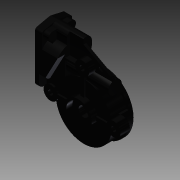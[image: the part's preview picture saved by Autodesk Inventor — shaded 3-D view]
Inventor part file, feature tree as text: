
AUTODESK INVENTOR PART (.ipt)
format: ipt  version: 2015 SP1 (Build 190203100, 203)  size: 293,888 bytes
history: native  units: in
note: dims shown in document units (in); Inventor stores cm internally (conversion verified against a paired STEP export)
features: fillet x1, other x1, imported_body x1
ambient origin geometry x8: Origin, YZ Plane, XZ Plane, XY Plane, X Axis, Y Axis, Z Axis, Center Point
bodies: Body1 (feature_tree)
feature tree (3):
  fillet  "Fillet1"  [1 undecoded]
  other  "AM-2235 gearbox housing.ipt1"
  imported_body  "Base1"
note: 1 required parameter value undecoded (feature->parameter linkage not recoverable at this tier; creation-order binding heuristic only, values carry confidence <= 0.55)
